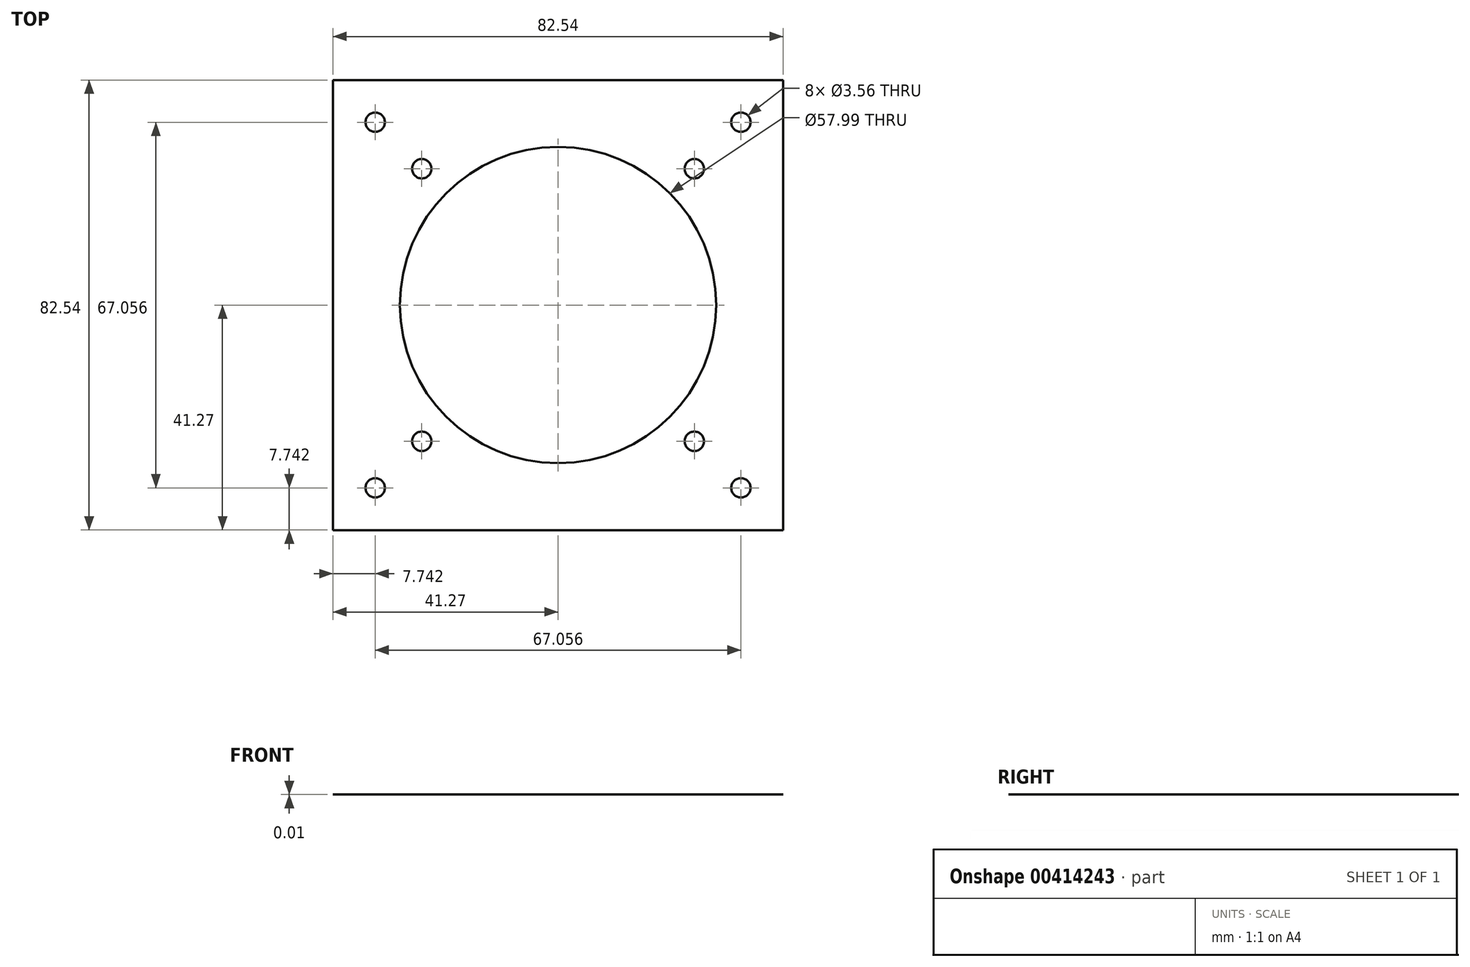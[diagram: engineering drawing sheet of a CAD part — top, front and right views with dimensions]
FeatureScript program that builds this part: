
annotation { "Feature Type Name" : "Feature", "Feature Type Description" : "" }
export const myFeature = defineFeature(function(context is Context, id is Id, definition is map)
    precondition{}
    {
        {
            var Q0;
            Q0=qCreatedBy(makeId("Top.planeOp"),FACE);
            var sketch = newSketch(context, id + "F0", { "sketchPlane" : qUnion([Q0])});
            skLineSegment(sketch, "E0.bottom", {"start": v(41.28, 41.28) * mm, "end": v(-41.28, 41.28) * mm});
            skLineSegment(sketch, "E0.top", {"start": v(41.28, -41.28) * mm, "end": v(-41.28, -41.28) * mm});
            skLineSegment(sketch, "E0.left", {"start": v(41.28, 41.28) * mm, "end": v(41.28, -41.28) * mm});
            skLineSegment(sketch, "E0.right", {"start": v(-41.28, 41.28) * mm, "end": v(-41.28, -41.28) * mm});
            skCircle(sketch, "E1", {"center": v(0, 0) * mm, "radius": 29 * mm});
            skLineSegment(sketch, "E2", {"start": v(0, 0) * mm, "end": v(0, 25) * mm, "construction": true});
            skLineSegment(sketch, "E3", {"start": v(0, 25) * mm, "end": v(25, 25) * mm, "construction": true});
            skCircle(sketch, "E4", {"center": v(25, 25) * mm, "radius": 1.78 * mm});
            skCircle(sketch, "E5.1.0", {"center": v(-25, 25) * mm, "radius": 1.78 * mm});
            skCircle(sketch, "E5.2.0", {"center": v(-25, -25) * mm, "radius": 1.78 * mm});
            skCircle(sketch, "E5.3.0", {"center": v(25, -25) * mm, "radius": 1.78 * mm});
            skLineSegment(sketch, "E6", {"start": v(0, 0) * mm, "end": v(41.28, 41.28) * mm, "construction": true});
            skCircle(sketch, "E7", {"center": v(33.53, 33.53) * mm, "radius": 1.78 * mm});
            skCircle(sketch, "E8.1.0", {"center": v(-33.53, 33.53) * mm, "radius": 1.78 * mm});
            skCircle(sketch, "E8.2.0", {"center": v(-33.53, -33.53) * mm, "radius": 1.78 * mm});
            skCircle(sketch, "E8.3.0", {"center": v(33.53, -33.53) * mm, "radius": 1.78 * mm});
            skLineSegment(sketch, "E9", {"start": v(0, 0) * mm, "end": v(41.28, 0) * mm, "construction": true});
            skSolve(sketch);
        }
        {
            var Q0;
            Q0=makeQuery(id+"F0.imprint","IMPRINT",FACE,{"disambiguationData":[TD([[makeQuery(id+"F0.imprint","IMPRINT",EDGE,{"derivedFrom":sQuery(id+"F0.wireOp",EDGE,"E0.bottom")}),1.0]])]});
            extrude(context, id + "F1", {"entities" : qUnion([Q0]), "depth" : 1 / 101.6 * mm});
        }
    });
